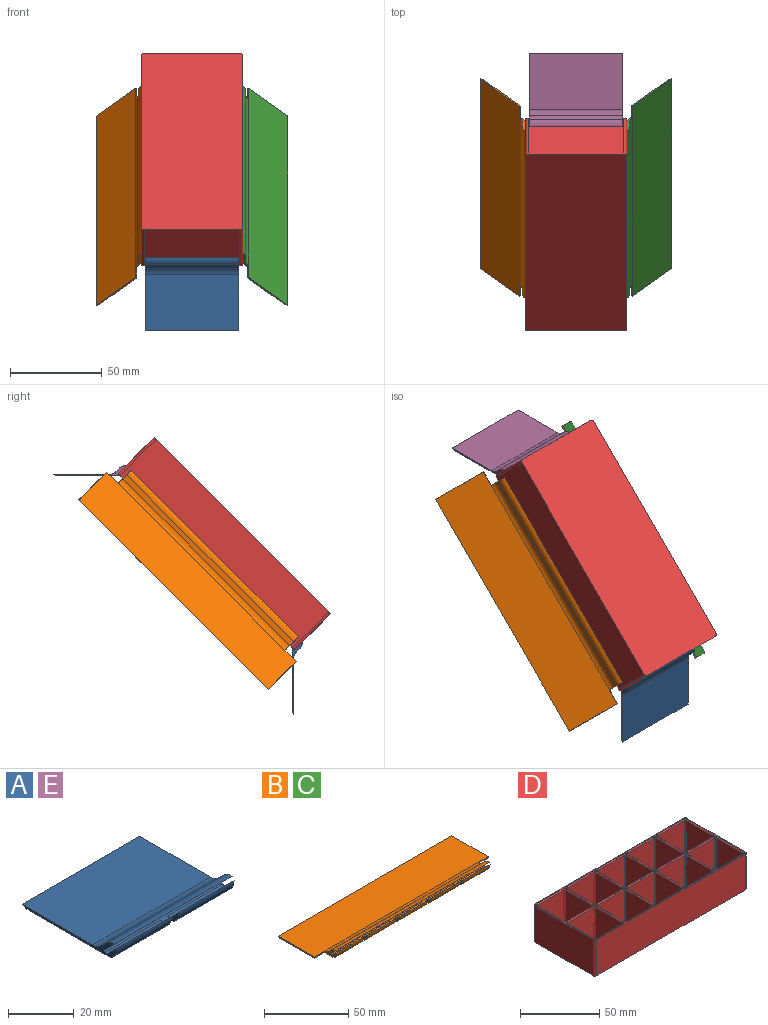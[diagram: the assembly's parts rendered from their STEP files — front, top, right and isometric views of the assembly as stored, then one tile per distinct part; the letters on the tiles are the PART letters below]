
ASSEMBLY  parts=5 mates=8
PART A: 20 faces, bbox 50.8x40.7x5.8 mm
  f0: plane 23.88x0.76mm, normal (0,-0.71,-0.71), area 25.6mm2, adj f2,f4,f10,f19
  f1: plane 23.88x3.66mm, normal (0,0.71,0.71), area 123.6mm2, adj f2,f3,f10,f19
  f2: cylinder r=5.08mm len=23.88mm, axis (-1,0,0), area 98.6mm2, adj f0,f1,f10,f19
  f3: cylinder r=0.79mm len=23.88mm, axis (-1,0,0), area 29.8mm2, adj f1,f8,f10,f19
  f4: plane 50.8x35.69mm, normal (0,0,-1), area 1808.1mm2, adj f0,f8,f9,f10,f13,f14,f18,f19
  f5: plane 50.8x30.47mm, normal (0,0,1), area 1547.6mm2, adj f9,f10,f12,f13
  f6: plane 50.8x2.07mm, normal (0,0.71,0.71), area 148.7mm2, adj f9,f10,f11,f12
  f7: plane 50.8x4.49mm, normal (0,-0.71,-0.71), area 322.6mm2, adj f8,f9,f10,f11
  f8: plane 50.8x1.35mm, normal (0,-0.71,0.71), area 40.7mm2, adj f3,f4,f7,f9,f10,f17,f18,f19
  f9: plane 40.67x5.84mm, normal (1,0,0), area 46.8mm2, adj f4,f5,f6,f7,f8,f11,f12,f13
  f10: plane 40.67x5.84mm, normal (-1,0,0), area 46.8mm2, adj f0,f1,f2,f3,f4,f5,f6,f7
  f11: cylinder r=5.08mm len=50.8mm, axis (1,0,0), area 209.7mm2, adj f6,f7,f9,f10
  f12: cylinder r=5.08mm len=50.8mm, axis (-1,0,0), area 202.7mm2, adj f5,f6,f9,f10
  f13: cylinder r=5.08mm len=50.8mm, axis (1,0,0), area 146.2mm2, adj f4,f5,f9,f10
  f14: plane 23.88x0.76mm, normal (0,-0.71,-0.71), area 25.6mm2, adj f4,f9,f16,f18
  f15: plane 23.88x3.66mm, normal (0,0.71,0.71), area 123.6mm2, adj f9,f16,f17,f18
  f16: cylinder r=5.08mm len=23.88mm, axis (-1,0,0), area 98.6mm2, adj f9,f14,f15,f18
  f17: cylinder r=0.79mm len=23.88mm, axis (-1,0,0), area 29.8mm2, adj f8,f9,f15,f18
  f18: plane 4.78x4.49mm, normal (-1,0,0), area 7.1mm2, adj f4,f8,f14,f15,f16,f17
  f19: plane 4.78x4.49mm, normal (1,0,0), area 7.1mm2, adj f0,f1,f2,f3,f4,f8
PART B: 42 faces, bbox 146.1x40.7x5.8 mm
  f0: plane 128.78x2.07mm, normal (0,0.71,0.71), area 376.9mm2, adj f3,f4,f38,f40
  f1: plane 128.78x4.49mm, normal (0,-0.71,-0.71), area 817.7mm2, adj f2,f3,f38,f40
  f2: plane 128.78x1.35mm, normal (0,-0.71,0.71), area 108.4mm2, adj f1,f9,f13,f14,f25,f26,f27,f30
  f3: cylinder r=5.08mm len=128.78mm, axis (1,0,0), area 531.7mm2, adj f0,f1,f38,f40
  f4: cylinder r=5.08mm len=128.78mm, axis (-1,0,0), area 513.8mm2, adj f0,f28,f38,f40
  f5: plane 30.47x0.79mm, normal (-1,0,0), area 23.5mm2, adj f14,f28,f29,f41
  f6: plane 22.57x0.76mm, normal (0,-0.71,-0.71), area 24.2mm2, adj f8,f14,f31,f40
  f7: plane 22.57x3.66mm, normal (0,0.71,0.71), area 116.8mm2, adj f8,f9,f31,f40
  f8: cylinder r=5.08mm len=22.57mm, axis (-1,0,0), area 93.2mm2, adj f6,f7,f31,f40
  f9: cylinder r=0.79mm len=22.57mm, axis (-1,0,0), area 28.1mm2, adj f2,f7,f31,f40
  f10: plane 22.58x0.76mm, normal (0,-0.71,-0.71), area 24.2mm2, adj f12,f14,f36,f38
  f11: plane 22.58x3.66mm, normal (0,0.71,0.71), area 116.9mm2, adj f12,f13,f36,f38
  f12: cylinder r=5.08mm len=22.58mm, axis (-1,0,0), area 93.2mm2, adj f10,f11,f36,f38
  f13: cylinder r=0.79mm len=22.58mm, axis (-1,0,0), area 28.2mm2, adj f2,f11,f36,f38
  f14: plane 146.05x35.69mm, normal (0,0,-1), area 5055mm2, adj f2,f5,f6,f10,f15,f16,f17,f18
  f15: plane 30.47x0.79mm, normal (1,0,0), area 23.5mm2, adj f14,f28,f29,f39
  f16: plane 23.81x0.76mm, normal (0,-0.71,-0.71), area 25.6mm2, adj f14,f22,f34,f37
  f17: plane 23.81x0.76mm, normal (0,-0.71,-0.71), area 25.6mm2, adj f14,f23,f32,f35
  f18: plane 23.81x0.76mm, normal (0,-0.71,-0.71), area 25.6mm2, adj f14,f24,f30,f33
  f19: plane 23.81x3.66mm, normal (0,0.71,0.71), area 123.2mm2, adj f22,f25,f34,f37
  f20: plane 23.81x3.66mm, normal (0,0.71,0.71), area 123.2mm2, adj f23,f26,f32,f35
  f21: plane 23.81x3.66mm, normal (0,0.71,0.71), area 123.2mm2, adj f24,f27,f30,f33
  f22: cylinder r=5.08mm len=23.81mm, axis (-1,0,0), area 98.3mm2, adj f16,f19,f34,f37
  f23: cylinder r=5.08mm len=23.81mm, axis (-1,0,0), area 98.3mm2, adj f17,f20,f32,f35
  f24: cylinder r=5.08mm len=23.81mm, axis (-1,0,0), area 98.3mm2, adj f18,f21,f30,f33
  f25: cylinder r=0.79mm len=23.81mm, axis (-1,0,0), area 29.7mm2, adj f2,f19,f34,f37
  f26: cylinder r=0.79mm len=23.81mm, axis (-1,0,0), area 29.7mm2, adj f2,f20,f32,f35
  f27: cylinder r=0.79mm len=23.81mm, axis (-1,0,0), area 29.7mm2, adj f2,f21,f30,f33
  f28: plane 146.05x30.47mm, normal (0,0,1), area 4449.4mm2, adj f4,f5,f15,f29,f39,f41
  f29: cylinder r=5.08mm len=146.05mm, axis (1,0,0), area 420.4mm2, adj f5,f14,f15,f28
  f30: plane 4.78x4.49mm, normal (-1,0,0), area 7.1mm2, adj f2,f14,f18,f21,f24,f27
  f31: plane 4.78x4.49mm, normal (1,0,0), area 7.1mm2, adj f2,f6,f7,f8,f9,f14
  f32: plane 4.78x4.49mm, normal (-1,0,0), area 7.1mm2, adj f2,f14,f17,f20,f23,f26
  f33: plane 4.78x4.49mm, normal (1,0,0), area 7.1mm2, adj f2,f14,f18,f21,f24,f27
  f34: plane 4.78x4.49mm, normal (-1,0,0), area 7.1mm2, adj f2,f14,f16,f19,f22,f25
  f35: plane 4.78x4.49mm, normal (1,0,0), area 7.1mm2, adj f2,f14,f17,f20,f23,f26
  f36: plane 4.78x4.49mm, normal (-1,0,0), area 7.1mm2, adj f2,f10,f11,f12,f13,f14
  f37: plane 4.78x4.49mm, normal (1,0,0), area 7.1mm2, adj f2,f14,f16,f19,f22,f25
  f38: plane 10.2x5.84mm, normal (1,0,0), area 23.4mm2, adj f0,f1,f2,f3,f4,f10,f11,f12
  f39: plane 8.64x0.79mm, normal (0,-1,0), area 6.9mm2, adj f14,f15,f28,f38
  f40: plane 10.2x5.84mm, normal (-1,0,0), area 23.4mm2, adj f0,f1,f2,f3,f4,f6,f7,f8
  f41: plane 8.64x0.79mm, normal (0,-1,0), area 6.9mm2, adj f5,f14,f28,f40
PART C: same geometry as B
PART D: 184 faces, bbox 136.1x55.4x27.8 mm
  f0: plane 2.55x2.55mm, normal (0,0,1), area 1.9mm2, adj f120,f125,f126,f129
  f1: plane 2.55x2.55mm, normal (0,0,1), area 1.9mm2, adj f171,f176,f177,f180
  f2: plane 2.55x2.55mm, normal (0,0,1), area 1.9mm2, adj f152,f157,f158,f162
  f3: plane 2.55x2.55mm, normal (0,0,1), area 1.9mm2, adj f136,f141,f142,f145
  f4: plane 26.2x23.81mm, normal (1,0,0), area 623.9mm2, adj f49,f100,f103,f179
  f5: plane 26.2x23.81mm, normal (0,-1,0), area 623.9mm2, adj f49,f100,f101,f167
  f6: plane 26.2x23.81mm, normal (-1,0,0), area 623.9mm2, adj f49,f101,f102,f175
  f7: plane 26.2x23.81mm, normal (0,-1,0), area 623.9mm2, adj f58,f96,f99,f114
  f8: plane 26.2x23.81mm, normal (-1,0,0), area 623.9mm2, adj f58,f96,f97,f106
  f9: plane 26.2x23.81mm, normal (0,1,0), area 623.9mm2, adj f58,f97,f98,f107
  f10: plane 26.2x23.81mm, normal (0,-1,0), area 623.9mm2, adj f57,f92,f95,f130
  f11: plane 26.2x23.81mm, normal (-1,0,0), area 623.9mm2, adj f57,f92,f93,f121
  f12: plane 26.2x23.81mm, normal (0,1,0), area 623.9mm2, adj f57,f93,f94,f122
  f13: plane 26.2x23.81mm, normal (0,1,0), area 623.9mm2, adj f56,f88,f91,f160
  f14: plane 26.2x23.81mm, normal (1,0,0), area 623.9mm2, adj f56,f88,f89,f173
  f15: plane 26.2x23.81mm, normal (0,-1,0), area 623.9mm2, adj f56,f89,f90,f181
  f16: plane 26.2x23.81mm, normal (0,1,0), area 623.9mm2, adj f55,f84,f87,f151
  f17: plane 26.2x23.81mm, normal (1,0,0), area 623.9mm2, adj f55,f84,f85,f150
  f18: plane 26.2x23.81mm, normal (0,-1,0), area 623.9mm2, adj f55,f85,f86,f139
  f19: plane 26.2x23.81mm, normal (0,1,0), area 623.9mm2, adj f54,f80,f83,f135
  f20: plane 26.2x23.81mm, normal (1,0,0), area 623.9mm2, adj f54,f80,f81,f134
  f21: plane 26.2x23.81mm, normal (0,-1,0), area 623.9mm2, adj f54,f81,f82,f123
  f22: plane 26.2x23.81mm, normal (0,1,0), area 623.9mm2, adj f53,f76,f79,f119
  f23: plane 26.2x23.81mm, normal (1,0,0), area 623.9mm2, adj f53,f76,f77,f118
  f24: plane 26.2x23.81mm, normal (0,-1,0), area 623.9mm2, adj f53,f77,f78,f108
  f25: plane 26.2x23.81mm, normal (0,1,0), area 623.9mm2, adj f52,f72,f75,f154
  f26: plane 26.2x23.81mm, normal (1,0,0), area 623.9mm2, adj f52,f72,f73,f164
  f27: plane 26.2x23.81mm, normal (0,-1,0), area 623.9mm2, adj f52,f73,f74,f163
  f28: plane 26.2x23.81mm, normal (1,0,0), area 623.9mm2, adj f51,f68,f71,f169
  f29: plane 26.2x23.81mm, normal (0,-1,0), area 623.9mm2, adj f51,f68,f69,f155
  f30: plane 26.2x23.81mm, normal (-1,0,0), area 623.9mm2, adj f51,f69,f70,f156
  f31: plane 52.32x27.78mm, normal (-1,0,0), area 1453.6mm2, adj f48,f59,f60,f63
  f32: plane 133.1x27.78mm, normal (0,-1,0), area 3697.6mm2, adj f48,f59,f60,f61
  f33: plane 52.32x27.78mm, normal (1,0,0), area 1453.6mm2, adj f48,f59,f61,f62
  f34: plane 26.2x23.81mm, normal (0,1,0), area 623.9mm2, adj f50,f64,f67,f138
  f35: plane 26.2x23.81mm, normal (1,0,0), area 623.9mm2, adj f50,f64,f65,f147
  f36: plane 26.2x23.81mm, normal (0,-1,0), area 623.9mm2, adj f50,f65,f66,f146
  f37: plane 26.2x23.81mm, normal (1,0,0), area 623.9mm2, adj f58,f98,f99,f115
  f38: plane 26.2x23.81mm, normal (1,0,0), area 623.9mm2, adj f57,f94,f95,f131
  f39: plane 26.2x23.81mm, normal (-1,0,0), area 623.9mm2, adj f56,f90,f91,f172
  f40: plane 26.2x23.81mm, normal (-1,0,0), area 623.9mm2, adj f55,f86,f87,f140
  f41: plane 26.2x23.81mm, normal (-1,0,0), area 623.9mm2, adj f54,f82,f83,f124
  f42: plane 26.2x23.81mm, normal (-1,0,0), area 623.9mm2, adj f53,f78,f79,f109
  f43: plane 26.2x23.81mm, normal (-1,0,0), area 623.9mm2, adj f52,f74,f75,f153
  f44: plane 26.2x23.81mm, normal (0,1,0), area 623.9mm2, adj f51,f70,f71,f170
  f45: plane 133.1x27.78mm, normal (0,1,0), area 3697.6mm2, adj f48,f59,f62,f63
  f46: plane 26.2x23.81mm, normal (-1,0,0), area 623.9mm2, adj f50,f66,f67,f137
  f47: plane 26.2x23.81mm, normal (0,1,0), area 623.9mm2, adj f49,f102,f103,f183
  f48: plane 136.14x55.37mm, normal (0,0,1), area 290.1mm2, adj f31,f32,f33,f45,f60,f61,f62,f63
  f49: plane 25.4x25.4mm, normal (0,0,1), area 644.6mm2, adj f4,f5,f6,f47,f100,f101,f102,f103
  f50: plane 25.4x25.4mm, normal (0,0,1), area 644.6mm2, adj f34,f35,f36,f46,f64,f65,f66,f67
  f51: plane 25.4x25.4mm, normal (0,0,1), area 644.6mm2, adj f28,f29,f30,f44,f68,f69,f70,f71
  f52: plane 25.4x25.4mm, normal (0,0,1), area 644.6mm2, adj f25,f26,f27,f43,f72,f73,f74,f75
  f53: plane 25.4x25.4mm, normal (0,0,1), area 644.6mm2, adj f22,f23,f24,f42,f76,f77,f78,f79
  f54: plane 25.4x25.4mm, normal (0,0,1), area 644.6mm2, adj f19,f20,f21,f41,f80,f81,f82,f83
  f55: plane 25.4x25.4mm, normal (0,0,1), area 644.6mm2, adj f16,f17,f18,f40,f84,f85,f86,f87
  f56: plane 25.4x25.4mm, normal (0,0,1), area 644.6mm2, adj f13,f14,f15,f39,f88,f89,f90,f91
  f57: plane 25.4x25.4mm, normal (0,0,1), area 644.6mm2, adj f10,f11,f12,f38,f92,f93,f94,f95
  f58: plane 25.4x25.4mm, normal (0,0,1), area 644.6mm2, adj f7,f8,f9,f37,f96,f97,f98,f99
  f59: plane 136.14x55.37mm, normal (0,0,-1), area 7536.6mm2, adj f31,f32,f33,f45,f60,f61,f62,f63
  f60: cylinder r=1.52mm len=27.78mm, axis (0,0,1), area 66.5mm2, adj f31,f32,f48,f59
  f61: cylinder r=1.52mm len=27.78mm, axis (0,0,-1), area 66.5mm2, adj f32,f33,f48,f59
  f62: cylinder r=1.52mm len=27.78mm, axis (0,0,1), area 66.5mm2, adj f33,f45,f48,f59
  f63: cylinder r=1.52mm len=27.78mm, axis (0,0,-1), area 66.5mm2, adj f31,f45,f48,f59
  f64: cylinder r=0.79mm len=26.2mm, axis (0,0,1), area 32.7mm2, adj f34,f35,f50,f143
  f65: cylinder r=0.79mm len=26.2mm, axis (0,0,1), area 32.7mm2, adj f35,f36,f50,f152
  f66: cylinder r=0.79mm len=26.2mm, axis (0,0,-1), area 32.7mm2, adj f36,f46,f50,f142
  f67: cylinder r=0.79mm len=26.2mm, axis (0,0,-1), area 32.7mm2, adj f34,f46,f50,f132
  f68: cylinder r=0.79mm len=26.2mm, axis (0,0,-1), area 32.7mm2, adj f28,f29,f51,f161
  f69: cylinder r=0.79mm len=26.2mm, axis (0,0,1), area 32.7mm2, adj f29,f30,f51,f149
  f70: cylinder r=0.79mm len=26.2mm, axis (0,0,-1), area 32.7mm2, adj f30,f44,f51,f162
  f71: cylinder r=0.79mm len=26.2mm, axis (0,0,1), area 32.7mm2, adj f28,f44,f51,f176
  f72: cylinder r=0.79mm len=26.2mm, axis (0,0,1), area 32.7mm2, adj f25,f26,f52,f159
  f73: cylinder r=0.79mm len=26.2mm, axis (0,0,1), area 32.7mm2, adj f26,f27,f52,f171
  f74: cylinder r=0.79mm len=26.2mm, axis (0,0,-1), area 32.7mm2, adj f27,f43,f52,f158
  f75: cylinder r=0.79mm len=26.2mm, axis (0,0,-1), area 32.7mm2, adj f25,f43,f52,f148
  f76: cylinder r=0.79mm len=26.2mm, axis (0,0,1), area 32.7mm2, adj f22,f23,f53,f125
  f77: cylinder r=0.79mm len=26.2mm, axis (0,0,-1), area 32.7mm2, adj f23,f24,f53,f112
  f78: cylinder r=0.79mm len=26.2mm, axis (0,0,1), area 32.7mm2, adj f24,f42,f53,f105
  f79: cylinder r=0.79mm len=26.2mm, axis (0,0,-1), area 32.7mm2, adj f22,f42,f53,f113
  f80: cylinder r=0.79mm len=26.2mm, axis (0,0,1), area 32.7mm2, adj f19,f20,f54,f141
  f81: cylinder r=0.79mm len=26.2mm, axis (0,0,-1), area 32.7mm2, adj f20,f21,f54,f128
  f82: cylinder r=0.79mm len=26.2mm, axis (0,0,1), area 32.7mm2, adj f21,f41,f54,f117
  f83: cylinder r=0.79mm len=26.2mm, axis (0,0,-1), area 32.7mm2, adj f19,f41,f54,f129
  f84: cylinder r=0.79mm len=26.2mm, axis (0,0,1), area 32.7mm2, adj f16,f17,f55,f157
  f85: cylinder r=0.79mm len=26.2mm, axis (0,0,-1), area 32.7mm2, adj f17,f18,f55,f144
  f86: cylinder r=0.79mm len=26.2mm, axis (0,0,1), area 32.7mm2, adj f18,f40,f55,f133
  f87: cylinder r=0.79mm len=26.2mm, axis (0,0,-1), area 32.7mm2, adj f16,f40,f55,f145
  f88: cylinder r=0.79mm len=26.2mm, axis (0,0,1), area 32.7mm2, adj f13,f14,f56,f166
  f89: cylinder r=0.79mm len=26.2mm, axis (0,0,1), area 32.7mm2, adj f14,f15,f56,f178
  f90: cylinder r=0.79mm len=26.2mm, axis (0,0,-1), area 32.7mm2, adj f15,f39,f56,f177
  f91: cylinder r=0.79mm len=26.2mm, axis (0,0,-1), area 32.7mm2, adj f13,f39,f56,f165
  f92: cylinder r=0.79mm len=26.2mm, axis (0,0,-1), area 32.7mm2, adj f10,f11,f57,f126
  f93: cylinder r=0.79mm len=26.2mm, axis (0,0,-1), area 32.7mm2, adj f11,f12,f57,f116
  f94: cylinder r=0.79mm len=26.2mm, axis (0,0,1), area 32.7mm2, adj f12,f38,f57,f127
  f95: cylinder r=0.79mm len=26.2mm, axis (0,0,1), area 32.7mm2, adj f10,f38,f57,f136
  f96: cylinder r=0.79mm len=26.2mm, axis (0,0,-1), area 32.7mm2, adj f7,f8,f58,f110
  f97: cylinder r=0.79mm len=26.2mm, axis (0,0,-1), area 32.7mm2, adj f8,f9,f58,f104
  f98: cylinder r=0.79mm len=26.2mm, axis (0,0,1), area 32.7mm2, adj f9,f37,f58,f111
  f99: cylinder r=0.79mm len=26.2mm, axis (0,0,1), area 32.7mm2, adj f7,f37,f58,f120
  f100: cylinder r=0.79mm len=26.2mm, axis (0,0,-1), area 32.7mm2, adj f4,f5,f49,f174
  f101: cylinder r=0.79mm len=26.2mm, axis (0,0,1), area 32.7mm2, adj f5,f6,f49,f168
  f102: cylinder r=0.79mm len=26.2mm, axis (0,0,-1), area 32.7mm2, adj f6,f47,f49,f180
  f103: cylinder r=0.79mm len=26.2mm, axis (0,0,1), area 32.7mm2, adj f4,f47,f49,f182
  f104: torus R=1.58mm, axis (0,0,1), area 2.1mm2, adj f48,f97,f106,f107
  f105: torus R=1.58mm, axis (0,0,1), area 2.1mm2, adj f48,f78,f108,f109
  f106: cylinder r=0.79mm len=23.81mm, axis (0,1,0), area 29.5mm2, adj f8,f48,f104,f110
  f107: cylinder r=0.79mm len=23.81mm, axis (1,0,0), area 29.5mm2, adj f9,f48,f104,f111
  f108: cylinder r=0.79mm len=23.81mm, axis (-1,0,0), area 29.5mm2, adj f24,f48,f105,f112
  f109: cylinder r=0.79mm len=23.81mm, axis (0,1,0), area 29.5mm2, adj f42,f48,f105,f113
  f110: torus R=1.58mm, axis (0,0,1), area 2.1mm2, adj f48,f96,f106,f113,f114
  f111: torus R=1.58mm, axis (0,0,1), area 2.1mm2, adj f48,f98,f107,f115,f116
  f112: torus R=1.58mm, axis (0,0,1), area 2.1mm2, adj f48,f77,f108,f117,f118
  f113: torus R=1.58mm, axis (0,0,1), area 2.1mm2, adj f48,f79,f109,f110,f119
  f114: cylinder r=0.79mm len=23.81mm, axis (-1,0,0), area 28.8mm2, adj f7,f110,f119,f120
  f115: cylinder r=0.79mm len=23.81mm, axis (0,-1,0), area 28.8mm2, adj f37,f111,f120,f121
  f116: torus R=1.58mm, axis (0,0,1), area 2.1mm2, adj f48,f93,f111,f121,f122
  f117: torus R=1.58mm, axis (0,0,1), area 2.1mm2, adj f48,f82,f112,f123,f124
  f118: cylinder r=0.79mm len=23.81mm, axis (0,-1,0), area 28.8mm2, adj f23,f112,f124,f125
  f119: cylinder r=0.79mm len=23.81mm, axis (1,0,0), area 28.8mm2, adj f22,f113,f114,f125
  f120: torus R=1.58mm, axis (0,0,1), area 2.1mm2, adj f0,f99,f114,f115,f125,f126
  f121: cylinder r=0.79mm len=23.81mm, axis (0,1,0), area 28.8mm2, adj f11,f115,f116,f126
  f122: cylinder r=0.79mm len=23.81mm, axis (1,0,0), area 29.5mm2, adj f12,f48,f116,f127
  f123: cylinder r=0.79mm len=23.81mm, axis (-1,0,0), area 29.5mm2, adj f21,f48,f117,f128
  f124: cylinder r=0.79mm len=23.81mm, axis (0,1,0), area 28.8mm2, adj f41,f117,f118,f129
  f125: torus R=1.58mm, axis (0,0,1), area 2.1mm2, adj f0,f76,f118,f119,f120,f129
  f126: torus R=1.58mm, axis (0,0,1), area 2.1mm2, adj f0,f92,f120,f121,f129,f130
  f127: torus R=1.58mm, axis (0,0,1), area 2.1mm2, adj f48,f94,f122,f131,f132
  f128: torus R=1.58mm, axis (0,0,1), area 2.1mm2, adj f48,f81,f123,f133,f134
  f129: torus R=1.58mm, axis (0,0,1), area 2.1mm2, adj f0,f83,f124,f125,f126,f135
  f130: cylinder r=0.79mm len=23.81mm, axis (-1,0,0), area 28.8mm2, adj f10,f126,f135,f136
  f131: cylinder r=0.79mm len=23.81mm, axis (0,-1,0), area 28.8mm2, adj f38,f127,f136,f137
  f132: torus R=1.58mm, axis (0,0,1), area 2.1mm2, adj f48,f67,f127,f137,f138
  f133: torus R=1.58mm, axis (0,0,1), area 2.1mm2, adj f48,f86,f128,f139,f140
  f134: cylinder r=0.79mm len=23.81mm, axis (0,-1,0), area 28.8mm2, adj f20,f128,f140,f141
  f135: cylinder r=0.79mm len=23.81mm, axis (1,0,0), area 28.8mm2, adj f19,f129,f130,f141
  f136: torus R=1.58mm, axis (0,0,1), area 2.1mm2, adj f3,f95,f130,f131,f141,f142
  f137: cylinder r=0.79mm len=23.81mm, axis (0,1,0), area 28.8mm2, adj f46,f131,f132,f142
  f138: cylinder r=0.79mm len=23.81mm, axis (1,0,0), area 29.5mm2, adj f34,f48,f132,f143
  f139: cylinder r=0.79mm len=23.81mm, axis (-1,0,0), area 29.5mm2, adj f18,f48,f133,f144
  f140: cylinder r=0.79mm len=23.81mm, axis (0,1,0), area 28.8mm2, adj f40,f133,f134,f145
  f141: torus R=1.58mm, axis (0,0,1), area 2.1mm2, adj f3,f80,f134,f135,f136,f145
  f142: torus R=1.58mm, axis (0,0,1), area 2.1mm2, adj f3,f66,f136,f137,f145,f146
  f143: torus R=1.58mm, axis (0,0,1), area 2.1mm2, adj f48,f64,f138,f147,f148
  f144: torus R=1.58mm, axis (0,0,1), area 2.1mm2, adj f48,f85,f139,f149,f150
  f145: torus R=1.58mm, axis (0,0,1), area 2.1mm2, adj f3,f87,f140,f141,f142,f151
  f146: cylinder r=0.79mm len=23.81mm, axis (-1,0,0), area 28.8mm2, adj f36,f142,f151,f152
  f147: cylinder r=0.79mm len=23.81mm, axis (0,-1,0), area 28.8mm2, adj f35,f143,f152,f153
  f148: torus R=1.58mm, axis (0,0,1), area 2.1mm2, adj f48,f75,f143,f153,f154
  f149: torus R=1.58mm, axis (0,0,1), area 2.1mm2, adj f48,f69,f144,f155,f156
  f150: cylinder r=0.79mm len=23.81mm, axis (0,-1,0), area 28.8mm2, adj f17,f144,f156,f157
  f151: cylinder r=0.79mm len=23.81mm, axis (1,0,0), area 28.8mm2, adj f16,f145,f146,f157
  f152: torus R=1.58mm, axis (0,0,1), area 2.1mm2, adj f2,f65,f146,f147,f157,f158
  f153: cylinder r=0.79mm len=23.81mm, axis (0,1,0), area 28.8mm2, adj f43,f147,f148,f158
  f154: cylinder r=0.79mm len=23.81mm, axis (1,0,0), area 29.5mm2, adj f25,f48,f148,f159
  f155: cylinder r=0.79mm len=23.81mm, axis (-1,0,0), area 29.5mm2, adj f29,f48,f149,f161
  f156: cylinder r=0.79mm len=23.81mm, axis (0,1,0), area 28.8mm2, adj f30,f149,f150,f162
  f157: torus R=1.58mm, axis (0,0,1), area 2.1mm2, adj f2,f84,f150,f151,f152,f162
  f158: torus R=1.58mm, axis (0,0,1), area 2.1mm2, adj f2,f74,f152,f153,f162,f163
  f159: torus R=1.58mm, axis (0,0,1), area 2.1mm2, adj f48,f72,f154,f164,f165
  f160: cylinder r=0.79mm len=23.81mm, axis (1,0,0), area 29.5mm2, adj f13,f48,f165,f166
  f161: torus R=1.58mm, axis (0,0,1), area 2.1mm2, adj f48,f68,f155,f168,f169
  f162: torus R=1.58mm, axis (0,0,1), area 2.1mm2, adj f2,f70,f156,f157,f158,f170
  f163: cylinder r=0.79mm len=23.81mm, axis (-1,0,0), area 28.8mm2, adj f27,f158,f170,f171
  f164: cylinder r=0.79mm len=23.81mm, axis (0,-1,0), area 28.8mm2, adj f26,f159,f171,f172
  f165: torus R=1.58mm, axis (0,0,1), area 2.1mm2, adj f48,f91,f159,f160,f172
  f166: torus R=1.58mm, axis (0,0,1), area 2.1mm2, adj f48,f88,f160,f173
  f167: cylinder r=0.79mm len=23.81mm, axis (-1,0,0), area 29.5mm2, adj f5,f48,f168,f174
  f168: torus R=1.58mm, axis (0,0,1), area 2.1mm2, adj f48,f101,f161,f167,f175
  f169: cylinder r=0.79mm len=23.81mm, axis (0,-1,0), area 28.8mm2, adj f28,f161,f175,f176
  f170: cylinder r=0.79mm len=23.81mm, axis (1,0,0), area 28.8mm2, adj f44,f162,f163,f176
  f171: torus R=1.58mm, axis (0,0,1), area 2.1mm2, adj f1,f73,f163,f164,f176,f177
  f172: cylinder r=0.79mm len=23.81mm, axis (0,1,0), area 28.8mm2, adj f39,f164,f165,f177
  f173: cylinder r=0.79mm len=23.81mm, axis (0,-1,0), area 29.5mm2, adj f14,f48,f166,f178
  f174: torus R=1.58mm, axis (0,0,1), area 2.1mm2, adj f48,f100,f167,f179
  f175: cylinder r=0.79mm len=23.81mm, axis (0,1,0), area 28.8mm2, adj f6,f168,f169,f180
  f176: torus R=1.58mm, axis (0,0,1), area 2.1mm2, adj f1,f71,f169,f170,f171,f180
  f177: torus R=1.58mm, axis (0,0,1), area 2.1mm2, adj f1,f90,f171,f172,f180,f181
  f178: torus R=1.58mm, axis (0,0,1), area 2.1mm2, adj f48,f89,f173,f181,f182
  f179: cylinder r=0.79mm len=23.81mm, axis (0,-1,0), area 29.5mm2, adj f4,f48,f174,f182
  f180: torus R=1.58mm, axis (0,0,1), area 2.1mm2, adj f1,f102,f175,f176,f177,f183
  f181: cylinder r=0.79mm len=23.81mm, axis (-1,0,0), area 28.8mm2, adj f15,f177,f178,f183
  f182: torus R=1.58mm, axis (0,0,1), area 2.1mm2, adj f48,f103,f178,f179,f183
  f183: cylinder r=0.79mm len=23.81mm, axis (1,0,0), area 28.8mm2, adj f47,f180,f181,f182
PART E: same geometry as A
PLACE A rot(axis=(0,-0.71,0.71),180deg) t=(-37.66,76.45,-183.84)mm
PLACE B rot(axis=(0,-0.71,0.71),90deg) t=(-117.59,91.8,-168.49)mm
PLACE C rot(axis=(0,0.71,-0.71),90deg) t=(-8.67,195.13,-65.16)mm
PLACE D rot(axis=(-0.68,0.68,0.28),148.6deg) t=(-35.44,165.6,-42.59)mm
PLACE E t=(-88.66,210.59,-49.71)mm
MATE planar A.f7 <-> D.f33  axis (0,0.71,0.71) through (-63.06,86.17,-155.69)mm
MATE planar C.f1 <-> D.f32  axis (-1,0,0) through (-35.44,134.28,-107.58)mm
MATE planar E.f7 <-> D.f31  axis (0,-0.71,-0.71) through (-63.26,182.44,-59.42)mm
MATE planar B.f1 <-> D.f45  axis (1,0,0) through (-90.82,134.22,-107.64)mm
MATE planar A.f8 <-> D.f3  axis (0,-0.71,0.71) through (-63.06,88.73,-157.62)mm
MATE planar D.f48 <-> C.f2  axis (0,0.71,-0.71) through (-36.18,144.97,-101.38)mm
MATE planar D.f3 <-> B.f2  axis (0,0.71,-0.71) through (-63.13,136.55,-109.8)mm
MATE planar E.f8 <-> D.f3  axis (0,-0.71,0.71) through (-88.66,184.42,-61.93)mm
